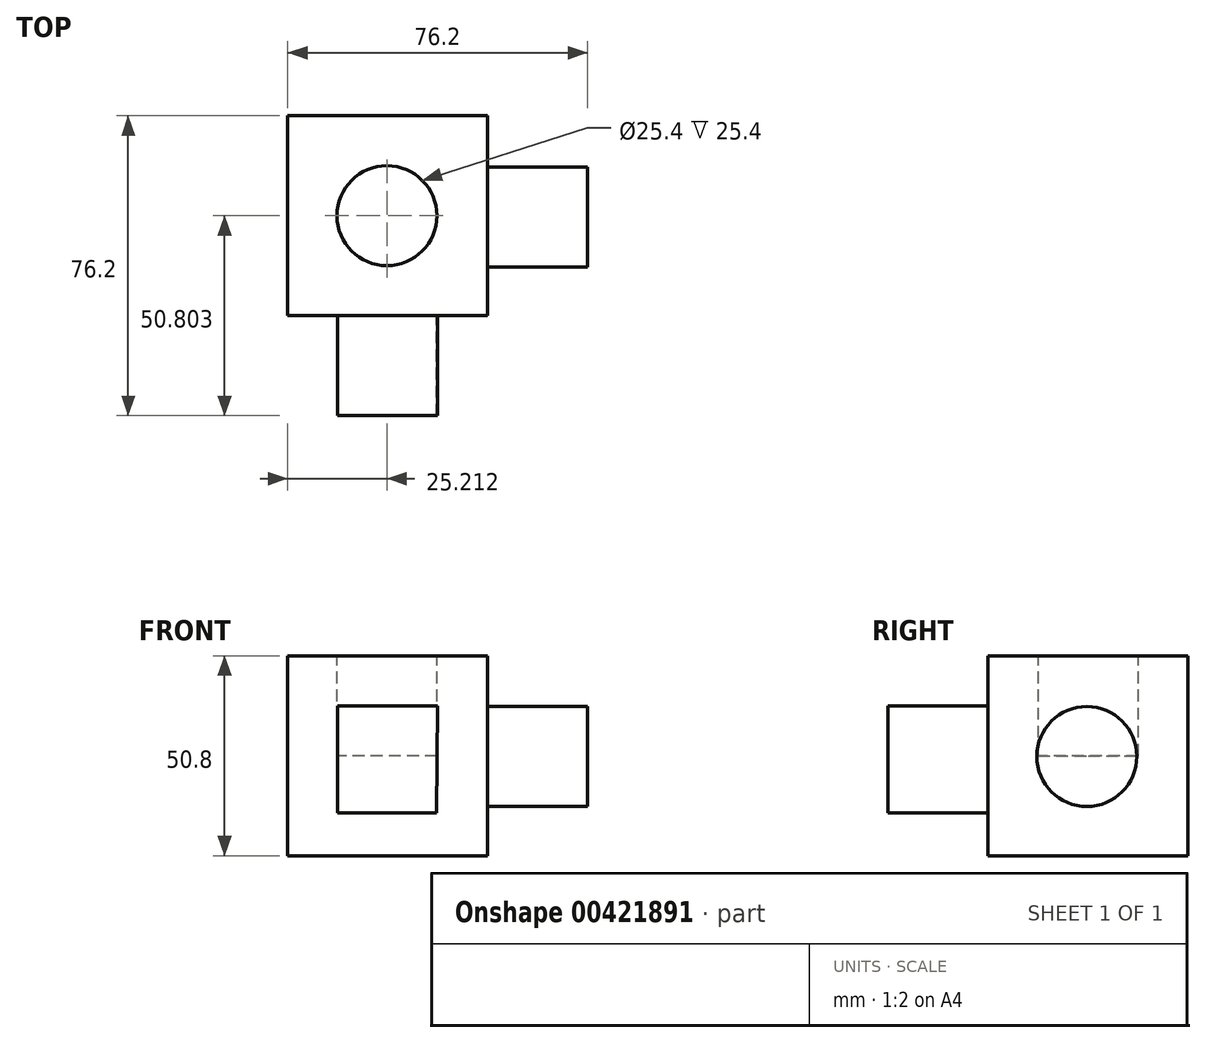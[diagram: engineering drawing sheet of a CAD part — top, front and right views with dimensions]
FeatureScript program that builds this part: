
annotation { "Feature Type Name" : "Feature", "Feature Type Description" : "" }
export const myFeature = defineFeature(function(context is Context, id is Id, definition is map)
    precondition{}
    {
        {
            var Q0;
            Q0=qCreatedBy(makeId("Front.planeOp"),FACE);
            var sketch = newSketch(context, id + "F0", { "sketchPlane" : qUnion([Q0])});
            skLineSegment(sketch, "E0", {"start": v(0, 0) * mm, "end": v(-50.8, 0) * mm});
            skLineSegment(sketch, "E1", {"start": v(-50.8, 0) * mm, "end": v(-50.8, 50.8) * mm});
            skLineSegment(sketch, "E2", {"start": v(-50.8, 50.8) * mm, "end": v(0, 50.8) * mm});
            skLineSegment(sketch, "E3", {"start": v(0, 50.8) * mm, "end": v(0, 0) * mm});
            skSolve(sketch);
        }
        {
            var Q0;
            Q0=makeQuery(id+"F0.imprint","IMPRINT",FACE,{"disambiguationData":[TD([[makeQuery(id+"F0.imprint","IMPRINT",EDGE,{"derivedFrom":sQuery(id+"F0.wireOp",EDGE,"E0")}),-1.0]])]});
            extrude(context, id + "F1", {"entities" : qUnion([Q0]), "depth" : 50.8 * mm});
        }
        {
            var Q0;
            Q0=makeQuery(id+"F1.opExtrude","CAP_FACE",FACE,{"disambiguationData":[OSD([sQuery(id+"F0.wireOp",EDGE,"E0"),sQuery(id+"F0.wireOp",EDGE,"E1"),sQuery(id+"F0.wireOp",EDGE,"E2"),sQuery(id+"F0.wireOp",EDGE,"E3")])],"isStart":false});
            var sketch = newSketch(context, id + "F2", { "sketchPlane" : qUnion([Q0])});
            skLineSegment(sketch, "E4", {"start": v(-38.1, 38.1) * mm, "end": v(-12.7, 38.1) * mm});
            skLineSegment(sketch, "E5", {"start": v(-38.1, 38.1) * mm, "end": v(-38.1, 10.88) * mm});
            skLineSegment(sketch, "E6", {"start": v(-38.1, 10.88) * mm, "end": v(-12.98, 10.88) * mm});
            skLineSegment(sketch, "E7", {"start": v(-12.98, 10.88) * mm, "end": v(-12.7, 38.1) * mm});
            skSolve(sketch);
        }
        {
            var Q0;
            Q0=makeQuery(id+"F2.imprint","IMPRINT",FACE,{"disambiguationData":[TD([[makeQuery(id+"F2.imprint","IMPRINT",EDGE,{"derivedFrom":sQuery(id+"F2.wireOp",EDGE,"E4")}),-1.0]])]});
            extrude(context, id + "F3", {"entities" : qUnion([Q0]), "operationType" : NewBodyOperationType.ADD, "depth" : 25.4 * mm});
        }
        {
            var Q0;
            Q0=makeQuery(id+"F1.opExtrude","SWEPT_FACE",FACE,{"disambiguationData":[OSD([sQuery(id+"F0.wireOp",EDGE,"E3")])]});
            var sketch = newSketch(context, id + "F4", { "sketchPlane" : qUnion([Q0])});
            skCircle(sketch, "E8", {"center": v(-25.74, 25.2) * mm, "radius": 12.7 * mm});
            skSolve(sketch);
        }
        {
            var Q0;
            Q0=makeQuery(id+"F4.imprint","IMPRINT",FACE,{"disambiguationData":[TD([[makeQuery(id+"F4.imprint","IMPRINT",EDGE,{"derivedFrom":sQuery(id+"F4.wireOp",EDGE,"E8")}),1.0]])]});
            extrude(context, id + "F5", {"entities" : qUnion([Q0]), "operationType" : NewBodyOperationType.ADD, "depth" : 25.4 * mm});
        }
        {
            var Q0;
            Q0=makeQuery(id+"F1.opExtrude","SWEPT_FACE",FACE,{"disambiguationData":[OSD([sQuery(id+"F0.wireOp",EDGE,"E2")])]});
            var sketch = newSketch(context, id + "F6", { "sketchPlane" : qUnion([Q0])});
            skCircle(sketch, "E9", {"center": v(-25.59, -25.4) * mm, "radius": 12.7 * mm});
            skSolve(sketch);
        }
        {
            var Q0;
            Q0=makeQuery(id+"F6.imprint","IMPRINT",FACE,{"disambiguationData":[TD([[makeQuery(id+"F6.imprint","IMPRINT",EDGE,{"derivedFrom":sQuery(id+"F6.wireOp",EDGE,"E9")}),1.0]])]});
            extrude(context, id + "F7", {"entities" : qUnion([Q0]), "operationType" : NewBodyOperationType.REMOVE, "oppositeDirection" : true, "depth" : 25.4 * mm});
        }
    });
